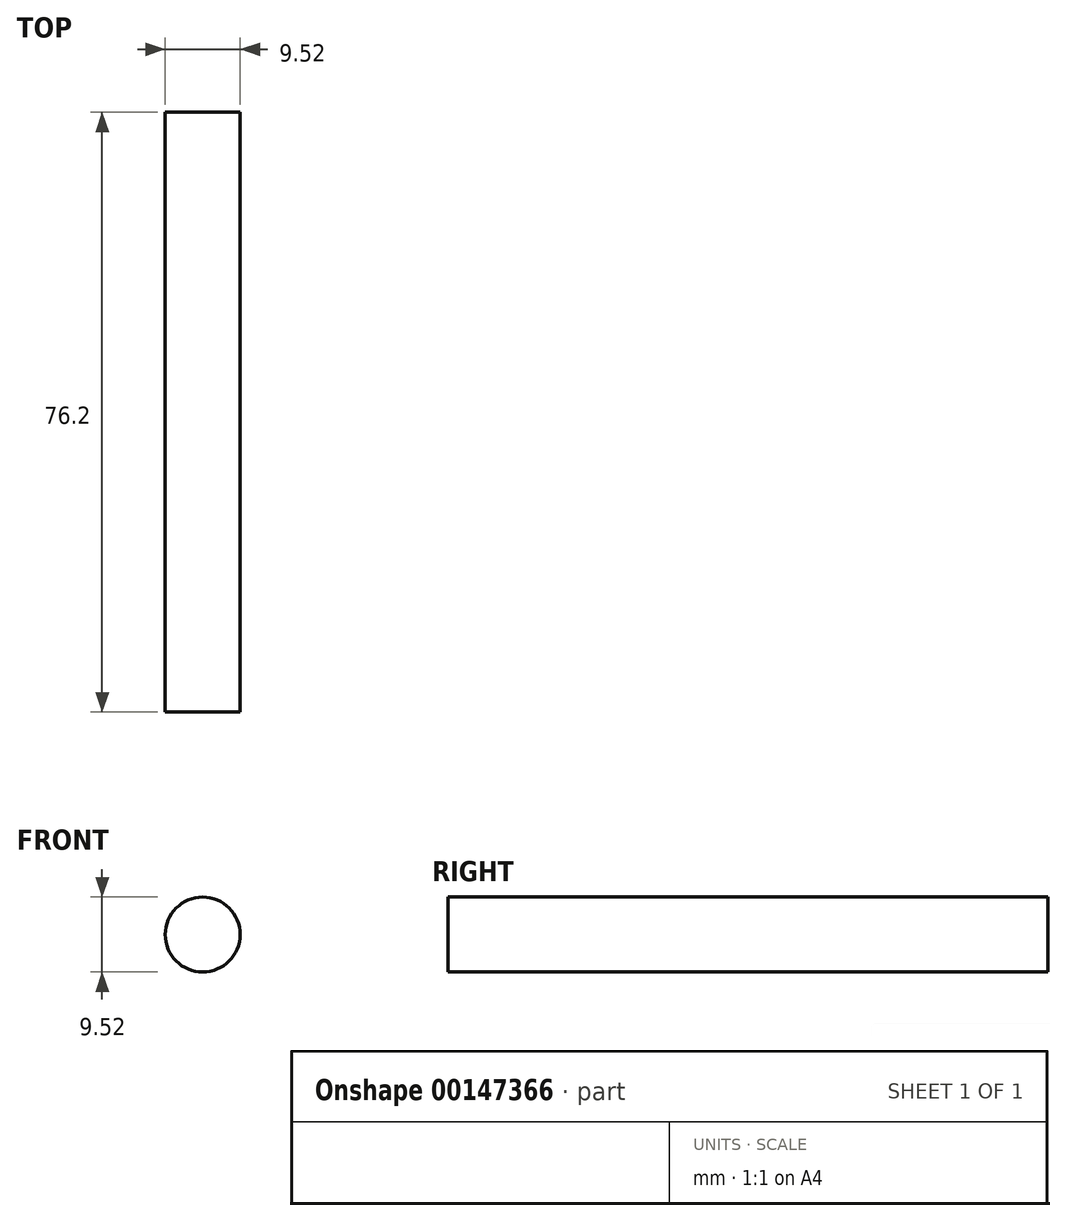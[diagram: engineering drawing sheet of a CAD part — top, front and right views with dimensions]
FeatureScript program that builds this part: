
annotation { "Feature Type Name" : "Feature", "Feature Type Description" : "" }
export const myFeature = defineFeature(function(context is Context, id is Id, definition is map)
    precondition{}
    {
        {
            var Q0;
            Q0=qCreatedBy(makeId("Front.planeOp"),FACE);
            var sketch = newSketch(context, id + "F0", { "sketchPlane" : qUnion([Q0])});
            skCircle(sketch, "E0", {"center": v(0, 0) * mm, "radius": 4.76 * mm});
            skSolve(sketch);
        }
        {
            var Q0;
            Q0 = qSketchRegion(id + "F0", true);
            extrude(context, id + "F1", {"entities" : qUnion([Q0]), "depth" : 76.2 * mm});
        }
    });
